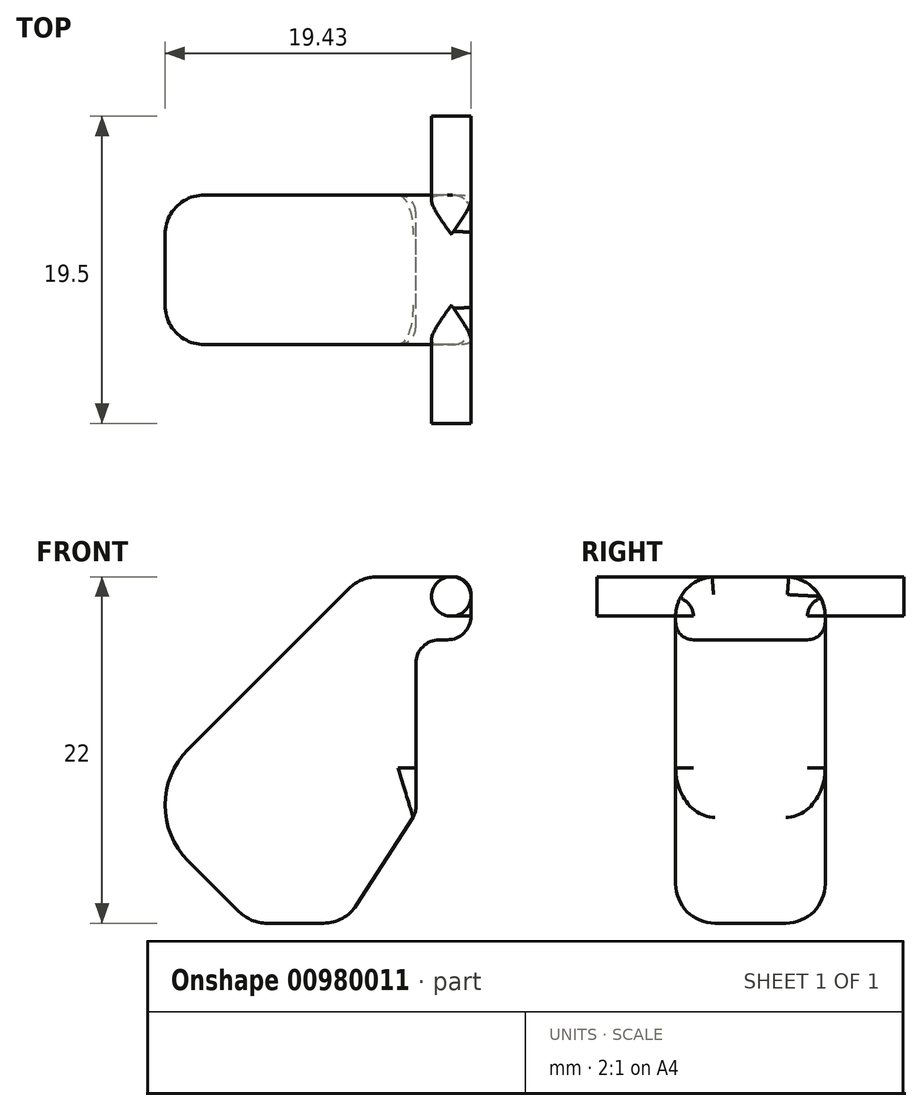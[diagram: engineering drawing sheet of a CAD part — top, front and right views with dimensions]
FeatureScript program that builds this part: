
annotation { "Feature Type Name" : "Feature", "Feature Type Description" : "" }
export const myFeature = defineFeature(function(context is Context, id is Id, definition is map)
    precondition{}
    {
        {
            var Q0;
            Q0=qCreatedBy(makeId("Front.planeOp"),FACE);
            var sketch = newSketch(context, id + "F0", { "sketchPlane" : qUnion([Q0])});
            skLineSegment(sketch, "E0", {"start": v(0, 0) * mm, "end": v(-6, 0) * mm});
            skLineSegment(sketch, "E1", {"start": v(-6, 0) * mm, "end": v(-13.5, 7.5) * mm});
            skLineSegment(sketch, "E2", {"start": v(-13.5, 7.5) * mm, "end": v(1, 22) * mm});
            skLineSegment(sketch, "E3", {"start": v(1, 22) * mm, "end": v(8, 22) * mm});
            skLineSegment(sketch, "E4", {"start": v(8, 22) * mm, "end": v(8, 18) * mm});
            skLineSegment(sketch, "E5", {"start": v(8, 18) * mm, "end": v(4.5, 18) * mm});
            skLineSegment(sketch, "E6", {"start": v(4.5, 18) * mm, "end": v(4.5, 7) * mm});
            skLineSegment(sketch, "E7", {"start": v(4.5, 7) * mm, "end": v(0, 0) * mm});
            skLineSegment(sketch, "E8", {"start": v(0, 0) * mm, "end": v(8, 0) * mm, "construction": true});
            skLineSegment(sketch, "E9", {"start": v(8, 0) * mm, "end": v(8, 18) * mm, "construction": true});
            skSolve(sketch);
        }
        {
            var Q0;
            Q0=makeQuery(id+"F0.imprint","IMPRINT",FACE,{"disambiguationData":[TD([[makeQuery(id+"F0.imprint","IMPRINT",EDGE,{"derivedFrom":sQuery(id+"F0.wireOp",EDGE,"E0")}),-1.0]])]});
            extrude(context, id + "F1", {"entities" : qUnion([Q0]), "depth" : 9.5 * mm, "offsetDistance" : 25 * mm});
        }
        {
            var Q0;
            {var subQ0=sQuery(id+"F0.wireOp",EDGE,"E2");var subQ1=sQuery(id+"F0.wireOp",EDGE,"E1");Q0=makeQuery(id+"F3.opFillet","BLEND_FACE",FACE,{"disambiguationData":[OSD([subQ1,subQ0]),TDD([makeQuery(id+"F1.opExtrude","SWEPT_EDGE",EDGE,{"disambiguationData":[OSD([subQ1,subQ0])]})])]});}
            var Q1;
            Q1=makeQuery(id+"F1.opExtrude","SWEPT_EDGE",EDGE,{"disambiguationData":[OSD([sQuery(id+"F0.wireOp",EDGE,"E1"),sQuery(id+"F0.wireOp",EDGE,"E2")])]});
            fillet(context, id + "F2", {"entities" : qUnion([Q0, Q1]), "radius" : 5 * mm, "tangentPropagation" : true, "allowEdgeOverflow" : false});
        }
        {
            var Q0;
            Q0=makeQuery(id+"F1.opExtrude","CAP_EDGE",EDGE,{"disambiguationData":[OSD([sQuery(id+"F0.wireOp",EDGE,"E1")])],"isStart":false});
            var Q1;
            Q1=makeQuery(id+"F1.opExtrude","CAP_EDGE",EDGE,{"disambiguationData":[OSD([sQuery(id+"F0.wireOp",EDGE,"E1")])],"isStart":true});
            var Q2;
            Q2=makeQuery(id+"F1.opExtrude","SWEPT_EDGE",EDGE,{"disambiguationData":[OSD([sQuery(id+"F0.wireOp",EDGE,"E0"),sQuery(id+"F0.wireOp",EDGE,"E1")])]});
            var Q3;
            Q3=makeQuery(id+"F1.opExtrude","CAP_EDGE",EDGE,{"disambiguationData":[OSD([sQuery(id+"F0.wireOp",EDGE,"E7")])],"isStart":false});
            var Q4;
            Q4=makeQuery(id+"F1.opExtrude","CAP_EDGE",EDGE,{"disambiguationData":[OSD([sQuery(id+"F0.wireOp",EDGE,"E7")])],"isStart":true});
            var Q5;
            Q5=makeQuery(id+"F1.opExtrude","SWEPT_EDGE",EDGE,{"disambiguationData":[OSD([sQuery(id+"F0.wireOp",EDGE,"E0"),sQuery(id+"F0.wireOp",EDGE,"E7")])]});
            var Q6;
            Q6=makeQuery(id+"F1.opExtrude","CAP_EDGE",EDGE,{"disambiguationData":[OSD([sQuery(id+"F0.wireOp",EDGE,"E0")])],"isStart":true});
            var Q7;
            Q7=makeQuery(id+"F1.opExtrude","CAP_EDGE",EDGE,{"disambiguationData":[OSD([sQuery(id+"F0.wireOp",EDGE,"E0")])],"isStart":false});
            var Q8;
            {var subQ0=sQuery(id+"F0.wireOp",EDGE,"E1");Q8=makeQuery(id+"F2.opFillet","BLEND_EDGE",EDGE,{"blendedFrom":[makeQuery(id+"F1.opExtrude","SWEPT_EDGE",EDGE,{"disambiguationData":[OSD([subQ0,sQuery(id+"F0.wireOp",EDGE,"E2")])]}),makeQuery(id+"F1.opExtrude","SWEPT_FACE",FACE,{"disambiguationData":[OSD([subQ0])]})],"blendedInto":[makeQuery(id+"F1.opExtrude","SWEPT_FACE",FACE,{"disambiguationData":[OSD([subQ0])]})]});}
            var Q9;
            Q9=makeQuery(id+"F1.opExtrude","SWEPT_EDGE",EDGE,{"disambiguationData":[OSD([sQuery(id+"F0.wireOp",EDGE,"E2"),sQuery(id+"F0.wireOp",EDGE,"E3")])]});
            var Q10;
            Q10=makeQuery(id+"F1.opExtrude","CAP_EDGE",EDGE,{"disambiguationData":[OSD([sQuery(id+"F0.wireOp",EDGE,"E3")])],"isStart":false});
            var Q11;
            Q11=makeQuery(id+"F1.opExtrude","CAP_EDGE",EDGE,{"disambiguationData":[OSD([sQuery(id+"F0.wireOp",EDGE,"E3")])],"isStart":true});
            fillet(context, id + "F3", {"entities" : qUnion([Q0, Q1, Q2, Q3, Q4, Q5, Q6, Q7, Q8, Q9, Q10, Q11]), "radius" : 2.5 * mm, "tangentPropagation" : true, "allowEdgeOverflow" : false});
        }
        {
            var Q0;
            Q0=makeQuery(id+"F1.opExtrude","CAP_FACE",FACE,{"disambiguationData":[OSD([sQuery(id+"F0.wireOp",EDGE,"E0"),sQuery(id+"F0.wireOp",EDGE,"E1"),sQuery(id+"F0.wireOp",EDGE,"E2"),sQuery(id+"F0.wireOp",EDGE,"E3"),sQuery(id+"F0.wireOp",EDGE,"E4"),sQuery(id+"F0.wireOp",EDGE,"E5"),sQuery(id+"F0.wireOp",EDGE,"E6"),sQuery(id+"F0.wireOp",EDGE,"E7")])],"isStart":false});
            var sketch = newSketch(context, id + "F4", { "sketchPlane" : qUnion([Q0])});
            skCircle(sketch, "E10", {"center": v(6.75, 20.75) * mm, "radius": 1.25 * mm});
            skSolve(sketch);
        }
        {
            var Q0;
            {var subQ0=sQuery(id+"F4.wireOp",EDGE,"E10");var subQ1=sQuery(id+"F0.wireOp",EDGE,"E3");var subQ2=makeQuery(id+"F3.opFillet","BLEND_EDGE",EDGE,{"blendedFrom":[makeQuery(id+"F1.opExtrude","CAP_EDGE",EDGE,{"disambiguationData":[OSD([subQ1])],"isStart":false}),makeQuery(id+"F1.opExtrude","CAP_FACE",FACE,{"disambiguationData":[OSD([sQuery(id+"F0.wireOp",EDGE,"E0"),sQuery(id+"F0.wireOp",EDGE,"E1"),sQuery(id+"F0.wireOp",EDGE,"E2"),subQ1,sQuery(id+"F0.wireOp",EDGE,"E4"),sQuery(id+"F0.wireOp",EDGE,"E5"),sQuery(id+"F0.wireOp",EDGE,"E6"),sQuery(id+"F0.wireOp",EDGE,"E7")])],"isStart":false})],"blendedInto":[makeQuery(id+"F1.opExtrude","CAP_FACE",FACE,{"disambiguationData":[OSD([sQuery(id+"F0.wireOp",EDGE,"E0"),sQuery(id+"F0.wireOp",EDGE,"E1"),sQuery(id+"F0.wireOp",EDGE,"E2"),subQ1,sQuery(id+"F0.wireOp",EDGE,"E4"),sQuery(id+"F0.wireOp",EDGE,"E5"),sQuery(id+"F0.wireOp",EDGE,"E6"),sQuery(id+"F0.wireOp",EDGE,"E7")])],"isStart":false})]});var subQ3=makeQuery(id+"F4.imprint","INTERSECT",VERTEX,{"disambiguationData":[OD(0.0)],"derivedFrom":[subQ2,subQ0]});Q0=makeQuery(id+"F4.imprint","IMPRINT",FACE,{"disambiguationData":[TD([[makeQuery(id+"F4.imprint","IMPRINT",EDGE,{"disambiguationData":[TD([[subQ3,-1.0]])],"derivedFrom":subQ0}),1.0]])]});}
            var Q1;
            {var subQ0=sQuery(id+"F4.wireOp",EDGE,"E10");var subQ1=sQuery(id+"F0.wireOp",EDGE,"E3");var subQ2=makeQuery(id+"F3.opFillet","BLEND_EDGE",EDGE,{"blendedFrom":[makeQuery(id+"F1.opExtrude","CAP_EDGE",EDGE,{"disambiguationData":[OSD([subQ1])],"isStart":false}),makeQuery(id+"F1.opExtrude","CAP_FACE",FACE,{"disambiguationData":[OSD([sQuery(id+"F0.wireOp",EDGE,"E0"),sQuery(id+"F0.wireOp",EDGE,"E1"),sQuery(id+"F0.wireOp",EDGE,"E2"),subQ1,sQuery(id+"F0.wireOp",EDGE,"E4"),sQuery(id+"F0.wireOp",EDGE,"E5"),sQuery(id+"F0.wireOp",EDGE,"E6"),sQuery(id+"F0.wireOp",EDGE,"E7")])],"isStart":false})],"blendedInto":[makeQuery(id+"F1.opExtrude","CAP_FACE",FACE,{"disambiguationData":[OSD([sQuery(id+"F0.wireOp",EDGE,"E0"),sQuery(id+"F0.wireOp",EDGE,"E1"),sQuery(id+"F0.wireOp",EDGE,"E2"),subQ1,sQuery(id+"F0.wireOp",EDGE,"E4"),sQuery(id+"F0.wireOp",EDGE,"E5"),sQuery(id+"F0.wireOp",EDGE,"E6"),sQuery(id+"F0.wireOp",EDGE,"E7")])],"isStart":false})]});var subQ3=makeQuery(id+"F4.imprint","INTERSECT",VERTEX,{"disambiguationData":[OD(0.0)],"derivedFrom":[subQ2,subQ0]});Q1=makeQuery(id+"F4.imprint","IMPRINT",FACE,{"disambiguationData":[TD([[makeQuery(id+"F4.imprint","IMPRINT",EDGE,{"disambiguationData":[TD([[subQ3,1.0]])],"derivedFrom":subQ0}),1.0]])]});}
            extrude(context, id + "F5", {"entities" : qUnion([Q0, Q1]), "operationType" : NewBodyOperationType.ADD, "depth" : 5 * mm, "offsetDistance" : 25 * mm, "hasSecondDirection" : true, "secondDirectionOppositeDirection" : true, "secondDirectionDepth" : 14.5 * mm});
        }
        {
            var Q0;
            Q0=makeQuery(id+"F1.opExtrude","SWEPT_EDGE",EDGE,{"disambiguationData":[OSD([sQuery(id+"F0.wireOp",EDGE,"E5"),sQuery(id+"F0.wireOp",EDGE,"E6")])]});
            var Q1;
            Q1=makeQuery(id+"F1.opExtrude","SWEPT_EDGE",EDGE,{"disambiguationData":[OSD([sQuery(id+"F0.wireOp",EDGE,"E4"),sQuery(id+"F0.wireOp",EDGE,"E5")])]});
            fillet(context, id + "F6", {"entities" : qUnion([Q0, Q1]), "radius" : 1.5 * mm, "tangentPropagation" : true, "allowEdgeOverflow" : false});
        }
        {
            var Q0;
            Q0=makeQuery(id+"F1.opExtrude","SWEPT_EDGE",EDGE,{"disambiguationData":[OSD([sQuery(id+"F0.wireOp",EDGE,"E3"),sQuery(id+"F0.wireOp",EDGE,"E4")])]});
            fillet(context, id + "F7", {"entities" : qUnion([Q0]), "radius" : 1.12 * mm, "tangentPropagation" : true, "allowEdgeOverflow" : false});
        }
    });
